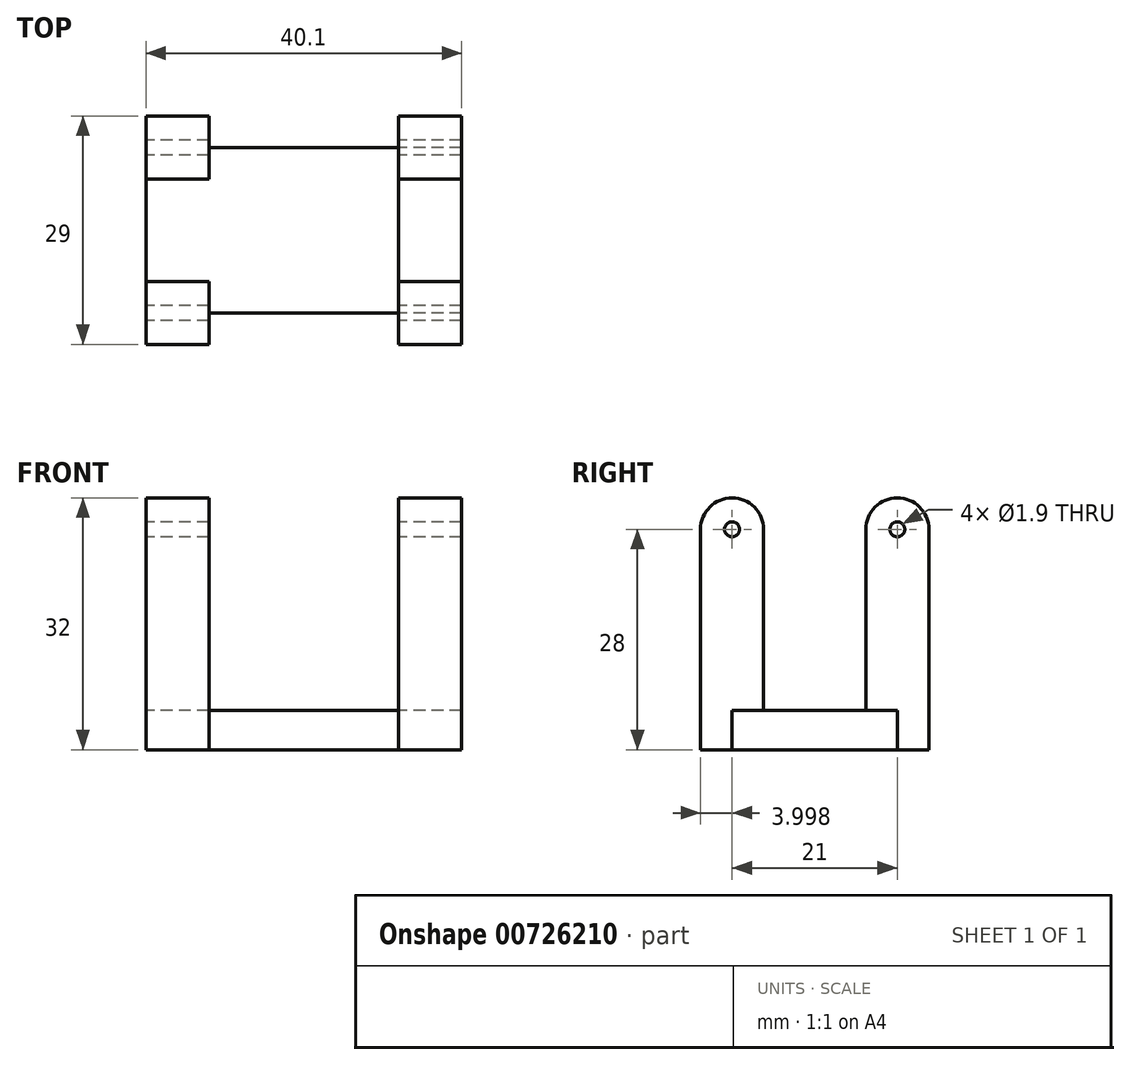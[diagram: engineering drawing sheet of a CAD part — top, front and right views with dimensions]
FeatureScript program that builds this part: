
annotation { "Feature Type Name" : "Feature", "Feature Type Description" : "" }
export const myFeature = defineFeature(function(context is Context, id is Id, definition is map)
    precondition{}
    {
        {
            var Q0;
            Q0=qCreatedBy(makeId("Top.planeOp"),FACE);
            var sketch = newSketch(context, id + "F0", { "sketchPlane" : qUnion([Q0])});
            skLineSegment(sketch, "E0.bottom", {"start": v(-4.86, 12.76) * mm, "end": v(19.34, 12.76) * mm});
            skLineSegment(sketch, "E0.top", {"start": v(-4.86, -8.24) * mm, "end": v(19.34, -8.24) * mm});
            skLineSegment(sketch, "E0.left", {"start": v(-4.86, 12.76) * mm, "end": v(-4.86, -8.24) * mm});
            skLineSegment(sketch, "E0.right", {"start": v(19.34, 12.76) * mm, "end": v(19.34, -8.24) * mm});
            skSolve(sketch);
        }
        {
            var Q0;
            Q0=makeQuery(id+"F0.imprint","IMPRINT",FACE,{"disambiguationData":[TD([[makeQuery(id+"F0.imprint","IMPRINT",EDGE,{"derivedFrom":sQuery(id+"F0.wireOp",EDGE,"E0.bottom")}),-1.0]])]});
            extrude(context, id + "F1", {"entities" : qUnion([Q0]), "depth" : 5 * mm, "offsetDistance" : 25 * mm});
        }
        {
            var Q0;
            Q0=makeQuery(id+"F1.opExtrude","SWEPT_FACE",FACE,{"disambiguationData":[OSD([sQuery(id+"F0.wireOp",EDGE,"E0.right")])]});
            var sketch = newSketch(context, id + "F2", { "sketchPlane" : qUnion([Q0])});
            skLineSegment(sketch, "E1", {"start": v(12.76, 5) * mm, "end": v(12.76, 28) * mm});
            skLineSegment(sketch, "E2", {"start": v(-8.24, 5) * mm, "end": v(-8.24, 28) * mm});
            skCircle(sketch, "E3", {"center": v(12.76, 28) * mm, "radius": 0.95 * mm});
            skCircle(sketch, "E4", {"center": v(-8.24, 28) * mm, "radius": 0.95 * mm});
            skCircle(sketch, "E5", {"center": v(12.76, 28) * mm, "radius": 4 * mm});
            skCircle(sketch, "E6", {"center": v(-8.24, 28) * mm, "radius": 4 * mm});
            skLineSegment(sketch, "E7", {"start": v(8.76, 28) * mm, "end": v(8.76, 5) * mm});
            skLineSegment(sketch, "E8", {"start": v(16.76, 28) * mm, "end": v(16.76, 0) * mm});
            skLineSegment(sketch, "E9", {"start": v(16.76, 0) * mm, "end": v(12.76, 0) * mm});
            skLineSegment(sketch, "E10", {"start": v(12.76, 0) * mm, "end": v(-8.24, 0) * mm});
            skLineSegment(sketch, "E11", {"start": v(-12.24, 28) * mm, "end": v(-12.24, 0) * mm});
            skLineSegment(sketch, "E12", {"start": v(-12.24, 0) * mm, "end": v(-8.24, 0) * mm});
            skLineSegment(sketch, "E13", {"start": v(-4.24, 28) * mm, "end": v(-4.24, 5) * mm});
            skSolve(sketch);
        }
        {
            var Q0;
            {var subQ6=sQuery(id+"F2.wireOp",EDGE,"E7");Q0=makeQuery(id+"F2.imprint","IMPRINT",FACE,{"disambiguationData":[TD([[makeQuery(id+"F2.imprint","IMPRINT",EDGE,{"derivedFrom":subQ6}),1.0]])]});}
            var Q1;
            {var subQ0=sQuery(id+"F2.wireOp",EDGE,"E8");Q1=makeQuery(id+"F2.imprint","IMPRINT",FACE,{"disambiguationData":[TD([[makeQuery(id+"F2.imprint","IMPRINT",EDGE,{"derivedFrom":subQ0}),-1.0]])]});}
            var Q2;
            Q2=makeQuery(id+"F2.imprint","IMPRINT",FACE,{"disambiguationData":[TD([[makeQuery(id+"F2.imprint","IMPRINT",EDGE,{"derivedFrom":sQuery(id+"F2.wireOp",EDGE,"E3")}),-1.0]])]});
            var Q3;
            Q3=makeQuery(id+"F2.imprint","IMPRINT",FACE,{"disambiguationData":[TD([[makeQuery(id+"F2.imprint","IMPRINT",EDGE,{"derivedFrom":sQuery(id+"F2.wireOp",EDGE,"E4")}),-1.0]])]});
            var Q4;
            {var subQ0=sQuery(id+"F2.wireOp",EDGE,"E11");Q4=makeQuery(id+"F2.imprint","IMPRINT",FACE,{"disambiguationData":[TD([[makeQuery(id+"F2.imprint","IMPRINT",EDGE,{"derivedFrom":subQ0}),1.0]])]});}
            var Q5;
            {var subQ6=sQuery(id+"F2.wireOp",EDGE,"E13");Q5=makeQuery(id+"F2.imprint","IMPRINT",FACE,{"disambiguationData":[TD([[makeQuery(id+"F2.imprint","IMPRINT",EDGE,{"derivedFrom":subQ6}),-1.0]])]});}
            extrude(context, id + "F3", {"entities" : qUnion([Q0, Q1, Q2, Q3, Q4, Q5]), "depth" : 8 * mm, "offsetDistance" : 25 * mm});
        }
        {
            var Q0;
            Q0=makeQuery(id+"F1.opExtrude","CAP_FACE",FACE,{"disambiguationData":[OSD([sQuery(id+"F0.wireOp",EDGE,"E0.bottom"),sQuery(id+"F0.wireOp",EDGE,"E0.top"),sQuery(id+"F0.wireOp",EDGE,"E0.left"),sQuery(id+"F0.wireOp",EDGE,"E0.right")])],"isStart":false});
            var sketch = newSketch(context, id + "F4", { "sketchPlane" : qUnion([Q0])});
            skLineSegment(sketch, "E14", {"start": v(7.24, 12.76) * mm, "end": v(7.24, -8.24) * mm});
            skSolve(sketch);
        }
        {
            var Q0;
            Q0=makeQuery(id+"F3.opExtrude","SWEPT_BODY",BODY,{"disambiguationData":[OSD([sQuery(id+"F0.wireOp",EDGE,"E0.bottom"),sQuery(id+"F0.wireOp",EDGE,"E0.right"),sQuery(id+"F2.wireOp",EDGE,"E3"),sQuery(id+"F2.wireOp",EDGE,"E5"),sQuery(id+"F2.wireOp",EDGE,"E7"),sQuery(id+"F2.wireOp",EDGE,"E8"),sQuery(id+"F2.wireOp",EDGE,"E9")])]});
            var Q1;
            Q1=makeQuery(id+"F3.opExtrude","SWEPT_BODY",BODY,{"disambiguationData":[OSD([sQuery(id+"F0.wireOp",EDGE,"E0.top"),sQuery(id+"F0.wireOp",EDGE,"E0.right"),sQuery(id+"F2.wireOp",EDGE,"E4"),sQuery(id+"F2.wireOp",EDGE,"E6"),sQuery(id+"F2.wireOp",EDGE,"E11"),sQuery(id+"F2.wireOp",EDGE,"E12"),sQuery(id+"F2.wireOp",EDGE,"E13")])]});
            transform(context, id + "F5", {"entities" : qUnion([Q0, Q1]), "transformType" : TransformType.TRANSLATION_3D, "dx" : -32.1 * mm, "dy" : 0 * mm, "dz" : 0 * mm, "makeCopy" : true});
        }
        {
            var Q0;
            Q0=makeQuery(id+"F5.opPattern","COPY",BODY,{"derivedFrom":makeQuery(id+"F3.opExtrude","SWEPT_BODY",BODY,{"disambiguationData":[OSD([sQuery(id+"F0.wireOp",EDGE,"E0.top"),sQuery(id+"F0.wireOp",EDGE,"E0.right"),sQuery(id+"F2.wireOp",EDGE,"E4"),sQuery(id+"F2.wireOp",EDGE,"E6"),sQuery(id+"F2.wireOp",EDGE,"E11"),sQuery(id+"F2.wireOp",EDGE,"E12"),sQuery(id+"F2.wireOp",EDGE,"E13")])]}),"instanceName":"1"});
            var Q1;
            Q1=makeQuery(id+"F5.opPattern","COPY",BODY,{"derivedFrom":makeQuery(id+"F3.opExtrude","SWEPT_BODY",BODY,{"disambiguationData":[OSD([sQuery(id+"F0.wireOp",EDGE,"E0.bottom"),sQuery(id+"F0.wireOp",EDGE,"E0.right"),sQuery(id+"F2.wireOp",EDGE,"E3"),sQuery(id+"F2.wireOp",EDGE,"E5"),sQuery(id+"F2.wireOp",EDGE,"E7"),sQuery(id+"F2.wireOp",EDGE,"E8"),sQuery(id+"F2.wireOp",EDGE,"E9")])]}),"instanceName":"1"});
            var Q2;
            Q2=makeQuery(id+"F3.opExtrude","SWEPT_BODY",BODY,{"disambiguationData":[OSD([sQuery(id+"F0.wireOp",EDGE,"E0.bottom"),sQuery(id+"F0.wireOp",EDGE,"E0.right"),sQuery(id+"F2.wireOp",EDGE,"E3"),sQuery(id+"F2.wireOp",EDGE,"E5"),sQuery(id+"F2.wireOp",EDGE,"E7"),sQuery(id+"F2.wireOp",EDGE,"E8"),sQuery(id+"F2.wireOp",EDGE,"E9")])]});
            var Q3;
            Q3=makeQuery(id+"F3.opExtrude","SWEPT_BODY",BODY,{"disambiguationData":[OSD([sQuery(id+"F0.wireOp",EDGE,"E0.top"),sQuery(id+"F0.wireOp",EDGE,"E0.right"),sQuery(id+"F2.wireOp",EDGE,"E4"),sQuery(id+"F2.wireOp",EDGE,"E6"),sQuery(id+"F2.wireOp",EDGE,"E11"),sQuery(id+"F2.wireOp",EDGE,"E12"),sQuery(id+"F2.wireOp",EDGE,"E13")])]});
            var Q4;
            Q4=makeQuery(id+"F1.opExtrude","SWEPT_BODY",BODY,{"disambiguationData":[OSD([sQuery(id+"F0.wireOp",EDGE,"E0.bottom"),sQuery(id+"F0.wireOp",EDGE,"E0.top"),sQuery(id+"F0.wireOp",EDGE,"E0.left"),sQuery(id+"F0.wireOp",EDGE,"E0.right")])]});
            booleanBodies(context, id + "F6", {"operationType" : BooleanOperationType.UNION, "tools" : qUnion([Q0, Q1, Q2, Q3, Q4])});
        }
        {
            var Q0;
            Q0=makeQuery(id+"F1.opExtrude","SWEPT_FACE",FACE,{"disambiguationData":[OSD([sQuery(id+"F0.wireOp",EDGE,"E0.left")])]});
            var Q1;
            Q1=makeQuery(id+"F5.opPattern","COPY",FACE,{"derivedFrom":makeQuery(id+"F3.opExtrude","CAP_FACE",FACE,{"disambiguationData":[OSD([sQuery(id+"F0.wireOp",EDGE,"E0.bottom"),sQuery(id+"F0.wireOp",EDGE,"E0.right"),sQuery(id+"F2.wireOp",EDGE,"E3"),sQuery(id+"F2.wireOp",EDGE,"E5"),sQuery(id+"F2.wireOp",EDGE,"E7"),sQuery(id+"F2.wireOp",EDGE,"E8"),sQuery(id+"F2.wireOp",EDGE,"E9")])],"isStart":true}),"instanceName":"1"});
            extrude(context, id + "F7", {"entities" : qUnion([Q0]), "operationType" : NewBodyOperationType.ADD, "endBound" : BoundingType.UP_TO_SURFACE, "depth" : 25 * mm, "endBoundEntityFace" : qUnion([Q1]), "offsetDistance" : 25 * mm});
        }
        {
            var Q0;
            Q0=makeQuery(id+"F1.opExtrude","SWEPT_FACE",FACE,{"disambiguationData":[OSD([sQuery(id+"F0.wireOp",EDGE,"E0.right")])]});
            var Q1;
            Q1=makeQuery(id+"F3.opExtrude","CAP_FACE",FACE,{"disambiguationData":[OSD([sQuery(id+"F0.wireOp",EDGE,"E0.top"),sQuery(id+"F0.wireOp",EDGE,"E0.right"),sQuery(id+"F2.wireOp",EDGE,"E4"),sQuery(id+"F2.wireOp",EDGE,"E6"),sQuery(id+"F2.wireOp",EDGE,"E11"),sQuery(id+"F2.wireOp",EDGE,"E12"),sQuery(id+"F2.wireOp",EDGE,"E13")])],"isStart":false});
            extrude(context, id + "F8", {"entities" : qUnion([Q0]), "endBound" : BoundingType.UP_TO_SURFACE, "depth" : 25 * mm, "endBoundEntityFace" : qUnion([Q1]), "offsetDistance" : 25 * mm});
        }
    });
